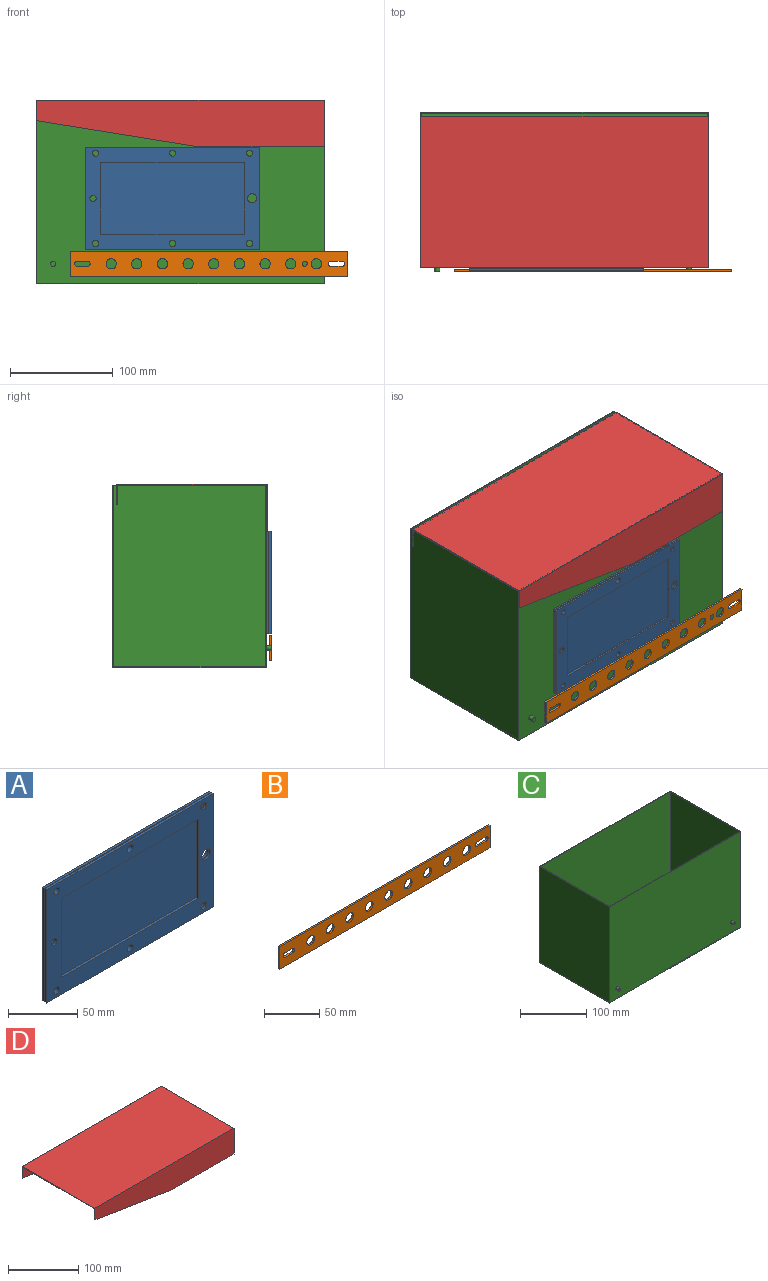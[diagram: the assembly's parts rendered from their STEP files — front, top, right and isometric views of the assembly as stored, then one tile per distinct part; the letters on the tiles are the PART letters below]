
ASSEMBLY  parts=4 mates=4
PART A: 40 faces, bbox 170x4.5x100 mm
  f0: plane 2x0.5mm, normal (1,0,0), area 1mm2, adj f3,f9,f19,f34
  f1: plane 37.26x0.5mm, normal (1,0,0), area 18.6mm2, adj f3,f9,f32,f34
  f2: plane 170x100mm, normal (0,-1,0), area 6938.5mm2, adj f10,f11,f12,f13,f14,f15,f16,f17
  f3: plane 170x100mm, normal (0,1,0), area 2163.2mm2, adj f0,f1,f4,f5,f6,f7,f10,f11
  f4: plane 39.34x0.5mm, normal (-1,0,0), area 19.7mm2, adj f3,f9,f35,f36
  f5: plane 2x0.5mm, normal (-1,0,0), area 1mm2, adj f3,f9,f19,f35
  f6: plane 39.34x0.5mm, normal (-1,0,0), area 19.7mm2, adj f3,f9,f33,f36
  f7: plane 37.26x0.5mm, normal (1,0,0), area 18.6mm2, adj f3,f9,f32,f37
  f8: plane 170x100mm, normal (0,1,0), area 6938.5mm2, adj f23,f24,f25,f26,f27,f28,f29,f30
  f9: plane 170x100mm, normal (0,-1,0), area 2163.2mm2, adj f0,f1,f4,f5,f6,f7,f18,f19
  f10: plane 170x2mm, normal (0,0,1), area 340mm2, adj f2,f3,f11,f17
  f11: plane 100x2mm, normal (-1,0,0), area 200mm2, adj f2,f3,f10,f12
  f12: plane 170x2mm, normal (0,0,-1), area 340mm2, adj f2,f3,f11,f17
  f13: plane 70x2mm, normal (1,0,0), area 140mm2, adj f2,f14,f16,f22
  f14: plane 140x2mm, normal (0,0,-1), area 280mm2, adj f2,f13,f15,f22
  f15: plane 70x2mm, normal (-1,0,0), area 140mm2, adj f2,f14,f16,f22
  f16: plane 140x2mm, normal (0,0,1), area 280mm2, adj f2,f13,f15,f22
  f17: plane 100x2mm, normal (1,0,0), area 200mm2, adj f2,f3,f10,f12
  f18: plane 2x0.5mm, normal (-1,0,0), area 1mm2, adj f3,f9,f21,f33
  f19: plane 150x0.5mm, normal (0,0,-1), area 75mm2, adj f0,f3,f5,f9
  f20: plane 2x0.5mm, normal (1,0,0), area 1mm2, adj f3,f9,f21,f37
  f21: plane 150x0.5mm, normal (0,0,1), area 75mm2, adj f3,f9,f18,f20
  f22: plane 140x70mm, normal (0,-1,0), area 9800mm2, adj f13,f14,f15,f16
  f23: plane 70x2mm, normal (-1,0,0), area 140mm2, adj f8,f24,f30,f31
  f24: plane 140x2mm, normal (0,0,-1), area 280mm2, adj f8,f23,f25,f31
  f25: plane 70x2mm, normal (1,0,0), area 140mm2, adj f8,f24,f30,f31
  f26: plane 170x2mm, normal (0,0,1), area 340mm2, adj f8,f9,f27,f29
  f27: plane 100x2mm, normal (1,0,0), area 200mm2, adj f8,f9,f26,f28
  f28: plane 170x2mm, normal (0,0,-1), area 340mm2, adj f8,f9,f27,f29
  f29: plane 100x2mm, normal (-1,0,0), area 200mm2, adj f8,f9,f26,f28
  f30: plane 140x2mm, normal (0,0,1), area 280mm2, adj f8,f23,f25,f31
  f31: plane 140x70mm, normal (0,1,0), area 9800mm2, adj f23,f24,f25,f30
  f32: cylinder r=4.5mm len=9mm, axis (0,-1,0), area 117.5mm2, adj f1,f2,f3,f7,f8,f9
  f33: cylinder r=3mm len=6mm, axis (0,-1,0), area 80.1mm2, adj f2,f3,f6,f8,f9,f18
  f34: cylinder r=3mm len=6mm, axis (0,-1,0), area 80.1mm2, adj f0,f1,f2,f3,f8,f9
  f35: cylinder r=3mm len=6mm, axis (0,-1,0), area 80.1mm2, adj f2,f3,f4,f5,f8,f9
  f36: cylinder r=3mm len=6mm, axis (0,-1,0), area 77.2mm2, adj f2,f3,f4,f6,f8,f9
  f37: cylinder r=3mm len=6mm, axis (0,-1,0), area 80.1mm2, adj f2,f3,f7,f8,f9,f20
  f38: cylinder r=3mm len=6mm, axis (0,-1,0), area 84.8mm2, adj f2,f8
  f39: cylinder r=3mm len=6mm, axis (0,-1,0), area 84.8mm2, adj f2,f8
PART B: 23 faces, bbox 270x2x25 mm
  f0: plane 270x2mm, normal (0,0,1), area 540mm2, adj f1,f20,f21,f22
  f1: plane 25x2mm, normal (-1,0,0), area 50mm2, adj f0,f2,f21,f22
  f2: plane 270x2mm, normal (0,0,-1), area 540mm2, adj f1,f20,f21,f22
  f3: cylinder r=2.5mm len=5mm, axis (0,1,0), area 15.7mm2, adj f4,f18,f21,f22
  f4: plane 11x2mm, normal (0,0,-1), area 22mm2, adj f3,f5,f21,f22
  f5: cylinder r=2.5mm len=5mm, axis (0,1,0), area 15.7mm2, adj f4,f18,f21,f22
  f6: cylinder r=2.5mm len=5mm, axis (0,1,0), area 15.7mm2, adj f7,f19,f21,f22
  f7: plane 10x2mm, normal (0,0,1), area 20mm2, adj f6,f8,f21,f22
  f8: cylinder r=2.5mm len=5mm, axis (0,1,0), area 15.7mm2, adj f7,f19,f21,f22
  f9: cylinder r=5mm len=10mm, axis (0,1,0), area 62.8mm2, adj f21,f22
  f10: cylinder r=5mm len=10mm, axis (0,1,0), area 62.8mm2, adj f21,f22
  f11: cylinder r=5mm len=10mm, axis (0,1,0), area 62.8mm2, adj f21,f22
  f12: cylinder r=5mm len=10mm, axis (0,1,0), area 62.8mm2, adj f21,f22
  f13: cylinder r=5mm len=10mm, axis (0,1,0), area 62.8mm2, adj f21,f22
  f14: cylinder r=5mm len=10mm, axis (0,1,0), area 62.8mm2, adj f21,f22
  f15: cylinder r=5mm len=10mm, axis (0,1,0), area 62.8mm2, adj f21,f22
  f16: cylinder r=5mm len=10mm, axis (0,1,0), area 62.8mm2, adj f21,f22
  f17: cylinder r=5mm len=10mm, axis (0,1,0), area 62.8mm2, adj f21,f22
  f18: plane 11x2mm, normal (0,0,1), area 22mm2, adj f3,f5,f21,f22
  f19: plane 10x2mm, normal (0,0,-1), area 20mm2, adj f6,f8,f21,f22
  f20: plane 25x2mm, normal (1,0,0), area 50mm2, adj f0,f2,f21,f22
  f21: plane 270x25mm, normal (0,-1,0), area 5898.9mm2, adj f0,f1,f2,f3,f4,f5,f6,f7
  f22: plane 270x25mm, normal (0,1,0), area 5898.9mm2, adj f0,f1,f2,f3,f4,f5,f6,f7
PART C: 15 faces, bbox 280x155x178 mm
  f0: plane 280x150mm, normal (0,0,1), area 856mm2, adj f1,f3,f4,f5,f6,f8,f9,f10
  f1: plane 178x150mm, normal (-1,0,0), area 26700mm2, adj f0,f2,f4,f5
  f2: plane 280x150mm, normal (0,0,-1), area 42000mm2, adj f1,f3,f4,f5
  f3: plane 178x150mm, normal (1,0,0), area 26700mm2, adj f0,f2,f4,f5
  f4: plane 280x178mm, normal (0,1,0), area 49840mm2, adj f0,f1,f2,f3
  f5: plane 280x178mm, normal (0,-1,0), area 49800.7mm2, adj f0,f1,f2,f3,f11,f13
  f6: plane 177x148mm, normal (1,0,0), area 26196mm2, adj f0,f7,f9,f10
  f7: plane 278x148mm, normal (0,0,1), area 41144mm2, adj f6,f8,f9,f10
  f8: plane 177x148mm, normal (-1,0,0), area 26196mm2, adj f0,f7,f9,f10
  f9: plane 278x177mm, normal (0,-1,0), area 49206mm2, adj f0,f6,f7,f8
  f10: plane 278x177mm, normal (0,1,0), area 49206mm2, adj f0,f6,f7,f8
  f11: cylinder r=2.5mm len=5mm, axis (0,1,0), area 78.5mm2, adj f5,f12
  f12: plane 5x5mm, normal (0,-1,0), area 19.6mm2, adj f11
  f13: cylinder r=2.5mm len=5mm, axis (0,1,0), area 78.5mm2, adj f5,f14
  f14: plane 5x5mm, normal (0,-1,0), area 19.6mm2, adj f13
PART D: 12 faces, bbox 280x147x45 mm
  f0: plane 147x45mm, normal (1,0,0), area 235mm2, adj f1,f4,f6,f7,f8,f9,f10,f11
  f1: plane 125x1mm, normal (0,0,-1), area 125mm2, adj f0,f2,f8,f11
  f2: plane 155x25mm, normal (-0.16,0,-0.99), area 157mm2, adj f1,f3,f8,f11
  f3: plane 147x20mm, normal (-1,0,0), area 185mm2, adj f2,f4,f5,f7,f8,f9,f10,f11
  f4: plane 280x147mm, normal (0,0,1), area 41160mm2, adj f0,f3,f7,f8
  f5: plane 155x25mm, normal (-0.16,0,-0.99), area 157mm2, adj f3,f6,f7,f10
  f6: plane 125x1mm, normal (0,0,-1), area 125mm2, adj f0,f5,f7,f10
  f7: plane 280x45mm, normal (0,-1,0), area 10662.5mm2, adj f0,f3,f4,f5,f6
  f8: plane 280x45mm, normal (0,1,0), area 10662.5mm2, adj f0,f1,f2,f3,f4
  f9: plane 280x145mm, normal (0,0,-1), area 40600mm2, adj f0,f3,f10,f11
  f10: plane 280x44mm, normal (0,1,0), area 10382.5mm2, adj f0,f3,f5,f6,f9
  f11: plane 280x44mm, normal (0,-1,0), area 10382.5mm2, adj f0,f1,f2,f3,f9
PLACE A t=(-7.55,-70.36,5.23)mm
PLACE B t=(27.6,-70.86,-58.56)mm
PLACE C t=(0.14,7.14,10.94)mm fixed
PLACE D t=(0.14,4.64,56.84)mm
MATE pin_slot B.f3 <-> C.f13  axis (0,-1,0) through (146.6,-72.86,-58.56)mm
MATE planar A.f39 <-> C.f5  axis (0,1,0) through (-7.55,-67.86,49.23)mm
MATE fastened D.f0 <-> C.f3  axis (1,0,0) through (140.14,-67.86,99.94)mm
MATE pin_slot B.f8 <-> C.f11  axis (0,-1,0) through (-100.4,-72.86,-58.56)mm
